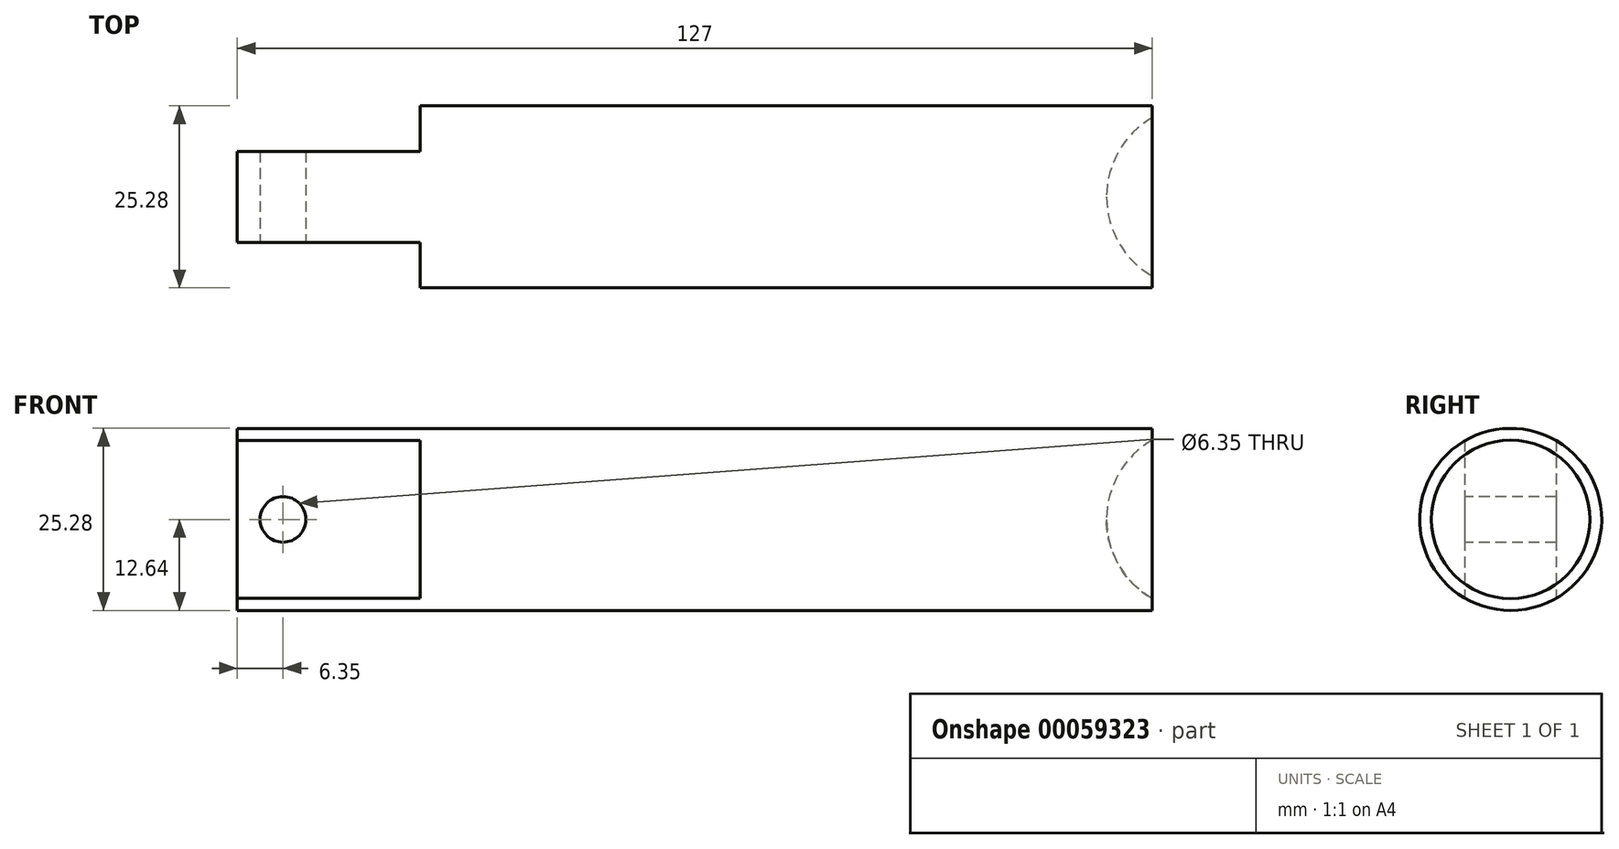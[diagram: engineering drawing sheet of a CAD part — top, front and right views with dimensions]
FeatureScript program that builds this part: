
annotation { "Feature Type Name" : "Feature", "Feature Type Description" : "" }
export const myFeature = defineFeature(function(context is Context, id is Id, definition is map)
    precondition{}
    {
        {
            var Q0;
            Q0=qCreatedBy(makeId("Right.planeOp"),FACE);
            var sketch = newSketch(context, id + "F0", { "sketchPlane" : qUnion([Q0])});
            skCircle(sketch, "E0", {"center": v(0, 0) * mm, "radius": 12.64 * mm});
            skSolve(sketch);
        }
        {
            var Q0;
            Q0 = qSketchRegion(id + "F0", true);
            extrude(context, id + "F1", {"entities" : qUnion([Q0]), "depth" : 127 * mm});
        }
        {
            var Q0;
            Q0=qCreatedBy(makeId("Right.planeOp"),FACE);
            var sketch = newSketch(context, id + "F2", { "sketchPlane" : qUnion([Q0])});
            skLineSegment(sketch, "E1.bottom", {"start": v(19, 24.47) * mm, "end": v(6.3, 24.47) * mm});
            skLineSegment(sketch, "E1.top", {"start": v(19, -24.45) * mm, "end": v(6.3, -24.45) * mm});
            skLineSegment(sketch, "E1.left", {"start": v(19, 24.47) * mm, "end": v(19, -24.45) * mm});
            skLineSegment(sketch, "E1.right", {"start": v(6.3, 24.47) * mm, "end": v(6.3, -24.45) * mm});
            skLineSegment(sketch, "E2.bottom", {"start": v(-6.35, 23.34) * mm, "end": v(-19.05, 23.34) * mm});
            skLineSegment(sketch, "E2.top", {"start": v(-6.35, -25) * mm, "end": v(-19.05, -25) * mm});
            skLineSegment(sketch, "E2.left", {"start": v(-6.35, 23.34) * mm, "end": v(-6.35, -25) * mm});
            skLineSegment(sketch, "E2.right", {"start": v(-19.05, 23.34) * mm, "end": v(-19.05, -25) * mm});
            skSolve(sketch);
        }
        {
            var Q0;
            Q0 = qSketchRegion(id + "F2", true);
            extrude(context, id + "F3", {"entities" : qUnion([Q0]), "operationType" : NewBodyOperationType.REMOVE, "depth" : 25.4 * mm});
        }
        {
            var Q0;
            Q0=qCreatedBy(makeId("Front.planeOp"),FACE);
            var sketch = newSketch(context, id + "F4", { "sketchPlane" : qUnion([Q0])});
            skCircle(sketch, "E3", {"center": v(6.35, 0) * mm, "radius": 3.18 * mm});
            skSolve(sketch);
        }
        {
            var Q0;
            Q0 = qSketchRegion(id + "F4", true);
            extrude(context, id + "F5", {"entities" : qUnion([Q0]), "operationType" : NewBodyOperationType.REMOVE, "endBound" : BoundingType.SYMMETRIC, "oppositeDirection" : true, "depth" : 25.4 * mm});
        }
        {
            var Q0;
            Q0=qCreatedBy(makeId("Front.planeOp"),FACE);
            var sketch = newSketch(context, id + "F6", { "sketchPlane" : qUnion([Q0])});
            skArc(sketch, "E4", {"start": v(146.05, 0) * mm, "mid": v(133.35, 12.7) * mm, "end": v(120.65, 0) * mm});
            skLineSegment(sketch, "E5", {"start": v(146.05, 0) * mm, "end": v(120.65, 0) * mm});
            skSolve(sketch);
        }
        {
            var Q0;
            Q0=makeQuery(id+"F6.imprint","IMPRINT",FACE,{"disambiguationData":[TD([[makeQuery(id+"F6.imprint","IMPRINT",EDGE,{"derivedFrom":sQuery(id+"F6.wireOp",EDGE,"E4")}),1.0]])]});
            var Q1;
            Q1=sQuery(id+"F6.wireOp",EDGE,"E5");
            revolve(context, id + "F7", {"operationType" : NewBodyOperationType.REMOVE, "entities" : qUnion([Q0]), "axis" : qUnion([Q1]), "revolveType" : RevolveType.FULL, "oppositeDirection" : true});
        }
    });
